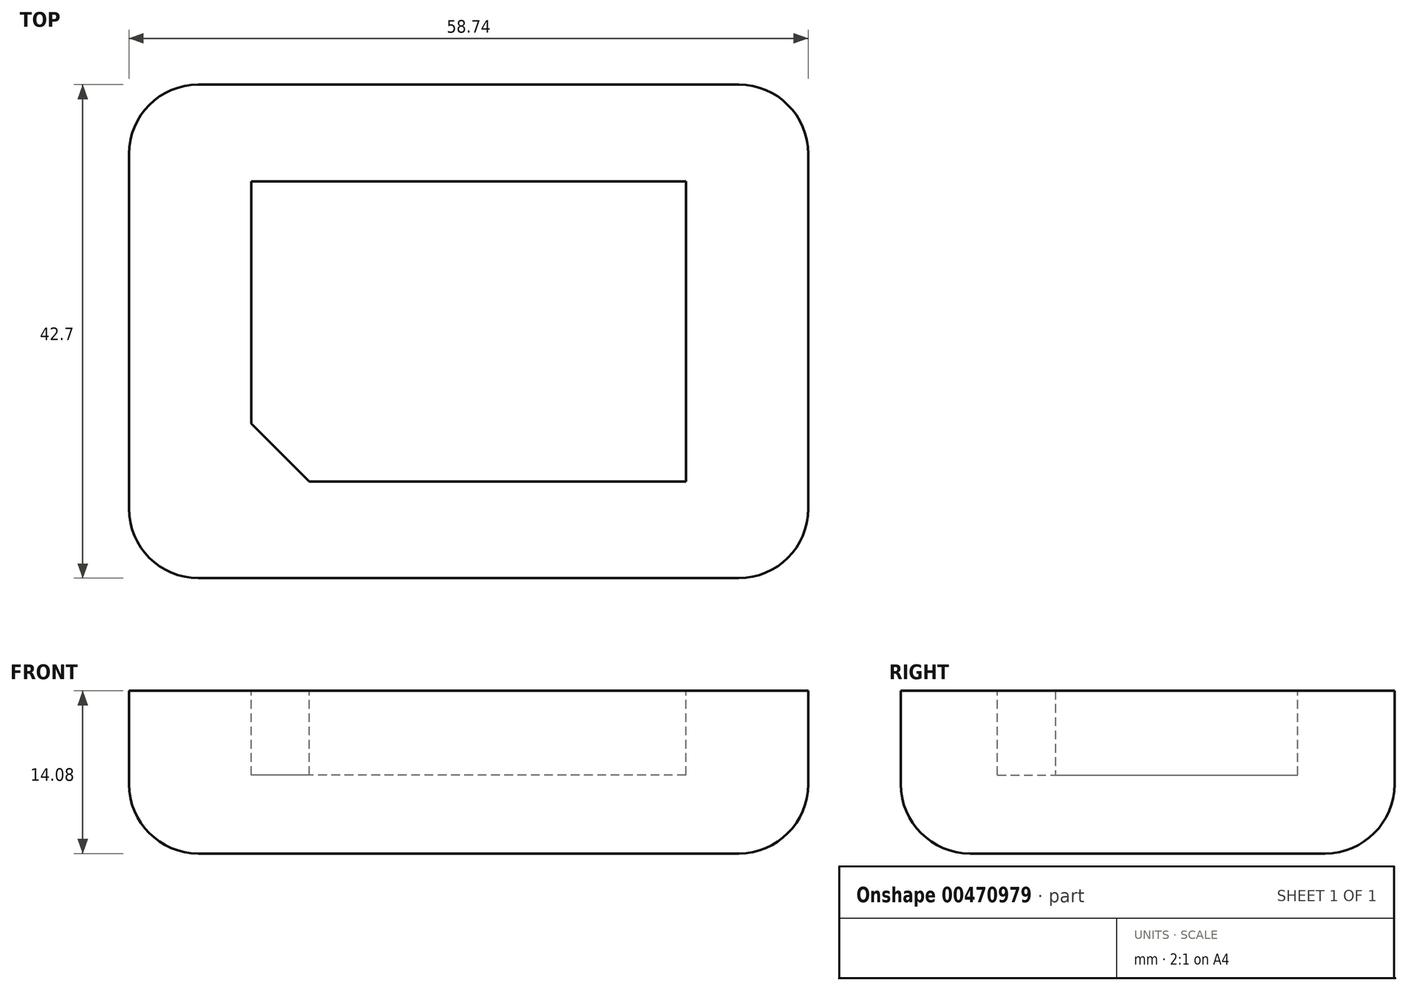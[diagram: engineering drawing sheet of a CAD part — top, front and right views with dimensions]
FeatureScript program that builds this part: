
annotation { "Feature Type Name" : "Feature", "Feature Type Description" : "" }
export const myFeature = defineFeature(function(context is Context, id is Id, definition is map)
    precondition{}
    {
        {
            var Q0;
            Q0=qCreatedBy(makeId("Top.planeOp"),FACE);
            var sketch = newSketch(context, id + "F0", { "sketchPlane" : qUnion([Q0])});
            skLineSegment(sketch, "E0.bottom", {"start": v(29.37, -21.35) * mm, "end": v(-29.37, -21.35) * mm});
            skLineSegment(sketch, "E0.top", {"start": v(29.37, 21.35) * mm, "end": v(-29.37, 21.35) * mm});
            skLineSegment(sketch, "E0.left", {"start": v(29.37, -21.35) * mm, "end": v(29.37, 21.35) * mm});
            skLineSegment(sketch, "E0.right", {"start": v(-29.37, -21.35) * mm, "end": v(-29.37, 21.35) * mm});
            skPoint(sketch, "E0.middle", {"position": v(0, 0) * mm});
            skSolve(sketch);
        }
        {
            var Q0;
            Q0 = qSketchRegion(id + "F0", true);
            extrude(context, id + "F1", {"entities" : qUnion([Q0]), "depth" : (7.04 * 2) * mm});
        }
        {
            var Q0;
            Q0=makeQuery(id+"F1.opExtrude","CAP_FACE",FACE,{"disambiguationData":[OSD([sQuery(id+"F0.wireOp",EDGE,"E0.bottom"),sQuery(id+"F0.wireOp",EDGE,"E0.top"),sQuery(id+"F0.wireOp",EDGE,"E0.left"),sQuery(id+"F0.wireOp",EDGE,"E0.right")])],"isStart":true});
            var Q1;
            Q1=makeQuery(id+"F1.opExtrude","SWEPT_EDGE",EDGE,{"disambiguationData":[OSD([sQuery(id+"F0.wireOp",EDGE,"E0.bottom"),sQuery(id+"F0.wireOp",EDGE,"E0.left")])]});
            var Q2;
            Q2=makeQuery(id+"F1.opExtrude","SWEPT_EDGE",EDGE,{"disambiguationData":[OSD([sQuery(id+"F0.wireOp",EDGE,"E0.top"),sQuery(id+"F0.wireOp",EDGE,"E0.left")])]});
            var Q3;
            Q3=makeQuery(id+"F1.opExtrude","SWEPT_EDGE",EDGE,{"disambiguationData":[OSD([sQuery(id+"F0.wireOp",EDGE,"E0.top"),sQuery(id+"F0.wireOp",EDGE,"E0.right")])]});
            var Q4;
            Q4=makeQuery(id+"F1.opExtrude","SWEPT_EDGE",EDGE,{"disambiguationData":[OSD([sQuery(id+"F0.wireOp",EDGE,"E0.bottom"),sQuery(id+"F0.wireOp",EDGE,"E0.right")])]});
            fillet(context, id + "F2", {"entities" : qUnion([Q0, Q1, Q2, Q3, Q4]), "radius" : 6 * mm, "tangentPropagation" : true, "allowEdgeOverflow" : false});
        }
        {
            var Q0;
            Q0=makeQuery(id+"F1.opExtrude","CAP_FACE",FACE,{"disambiguationData":[OSD([sQuery(id+"F0.wireOp",EDGE,"E0.bottom"),sQuery(id+"F0.wireOp",EDGE,"E0.top"),sQuery(id+"F0.wireOp",EDGE,"E0.left"),sQuery(id+"F0.wireOp",EDGE,"E0.right")])],"isStart":false});
            var sketch = newSketch(context, id + "F3", { "sketchPlane" : qUnion([Q0])});
            skLineSegment(sketch, "E1.bottom", {"start": v(18.79, -12.99) * mm, "end": v(-18.79, -12.99) * mm});
            skLineSegment(sketch, "E1.top", {"start": v(18.79, 12.99) * mm, "end": v(-18.79, 12.99) * mm});
            skLineSegment(sketch, "E1.left", {"start": v(18.79, -12.99) * mm, "end": v(18.79, 12.99) * mm});
            skLineSegment(sketch, "E1.right", {"start": v(-18.79, -12.99) * mm, "end": v(-18.79, 12.99) * mm});
            skPoint(sketch, "E1.middle", {"position": v(0, 0) * mm});
            skSolve(sketch);
        }
        {
            var Q0;
            Q0=makeQuery(id+"F3.imprint","IMPRINT",FACE,{"disambiguationData":[TD([[makeQuery(id+"F3.imprint","IMPRINT",EDGE,{"derivedFrom":sQuery(id+"F3.wireOp",EDGE,"E1.bottom")}),-1.0]])]});
            extrude(context, id + "F4", {"entities" : qUnion([Q0]), "operationType" : NewBodyOperationType.REMOVE, "oppositeDirection" : true, "depth" : 7.3 * mm});
        }
        {
            var Q0;
            Q0=makeQuery(id+"F4.boolean.opBoolean","COPY",EDGE,{"derivedFrom":makeQuery(id+"F4.opExtrude","SWEPT_EDGE",EDGE,{"disambiguationData":[OSD([sQuery(id+"F3.wireOp",EDGE,"E1.bottom"),sQuery(id+"F3.wireOp",EDGE,"E1.right")])]})});
            chamfer(context, id + "F5", {"entities" : qUnion([Q0]), "width" : 5 * mm, "tangentPropagation" : true});
        }
    });
